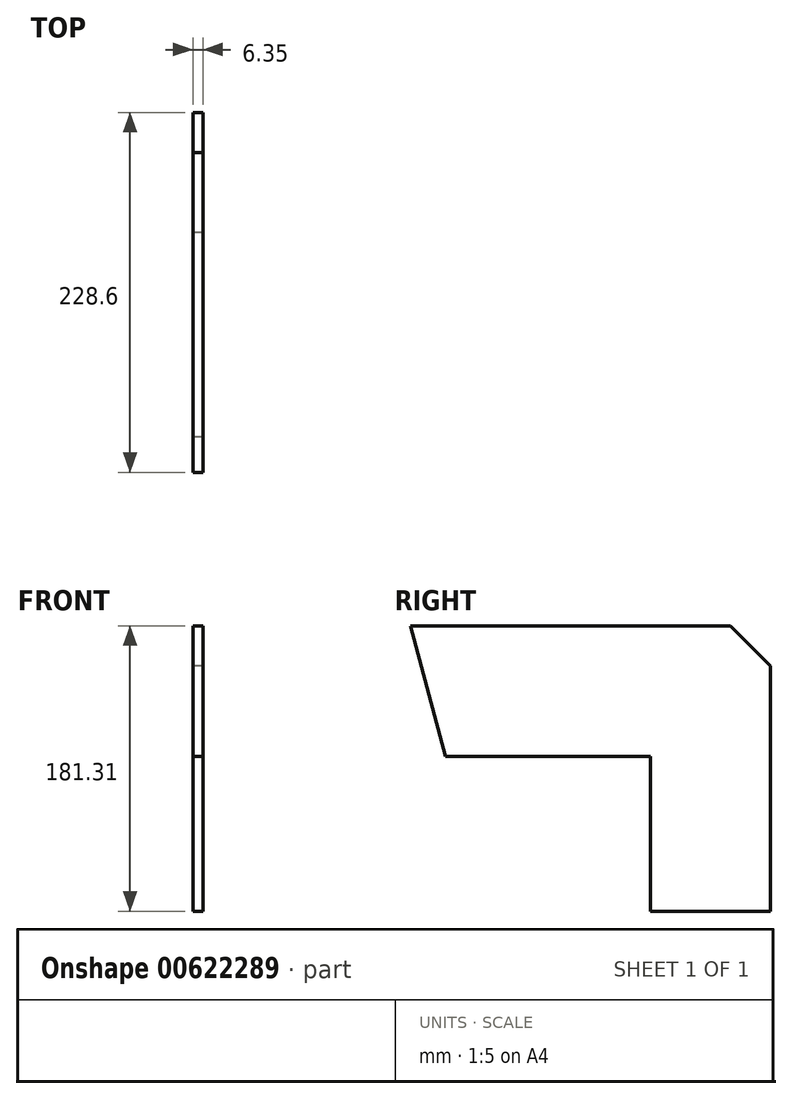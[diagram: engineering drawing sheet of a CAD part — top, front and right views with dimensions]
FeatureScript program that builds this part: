
annotation { "Feature Type Name" : "Feature", "Feature Type Description" : "" }
export const myFeature = defineFeature(function(context is Context, id is Id, definition is map)
    precondition{}
    {
        {
            var Q0;
            Q0=qCreatedBy(makeId("Right.planeOp"),FACE);
            var sketch = newSketch(context, id + "F0", { "sketchPlane" : qUnion([Q0])});
            skLineSegment(sketch, "E0.top", {"start": v(0, -98.26) * mm, "end": v(76.2, -98.26) * mm});
            skLineSegment(sketch, "E0.left", {"start": v(0, 0) * mm, "end": v(0, -98.26) * mm});
            skLineSegment(sketch, "E0.right", {"start": v(76.2, 0) * mm, "end": v(76.2, -98.26) * mm});
            skLineSegment(sketch, "E1.bottom", {"start": v(0, 0) * mm, "end": v(-130.15, 0) * mm});
            skLineSegment(sketch, "E1.top", {"start": v(50.8, 83.05) * mm, "end": v(-152.4, 83.05) * mm});
            skLineSegment(sketch, "E1.left", {"start": v(76.2, 0) * mm, "end": v(76.2, 57.65) * mm});
            skLineSegment(sketch, "E2", {"start": v(-152.4, 83.05) * mm, "end": v(-130.15, 0) * mm});
            skPoint(sketch, "E3", {"position": v(76.2, 57.65) * mm});
            skPoint(sketch, "E4", {"position": v(50.8, 83.05) * mm});
            skLineSegment(sketch, "E5", {"start": v(50.8, 83.05) * mm, "end": v(76.2, 57.65) * mm});
            skPoint(sketch, "E6.orphan", {"position": v(76.2, 83.05) * mm});
            skSolve(sketch);
        }
        {
            var Q0;
            Q0 = qSketchRegion(id + "F0", true);
            extrude(context, id + "F1", {"entities" : qUnion([Q0]), "depth" : 6.35 * mm, "offsetDistance" : 25.4 * mm});
        }
    });
